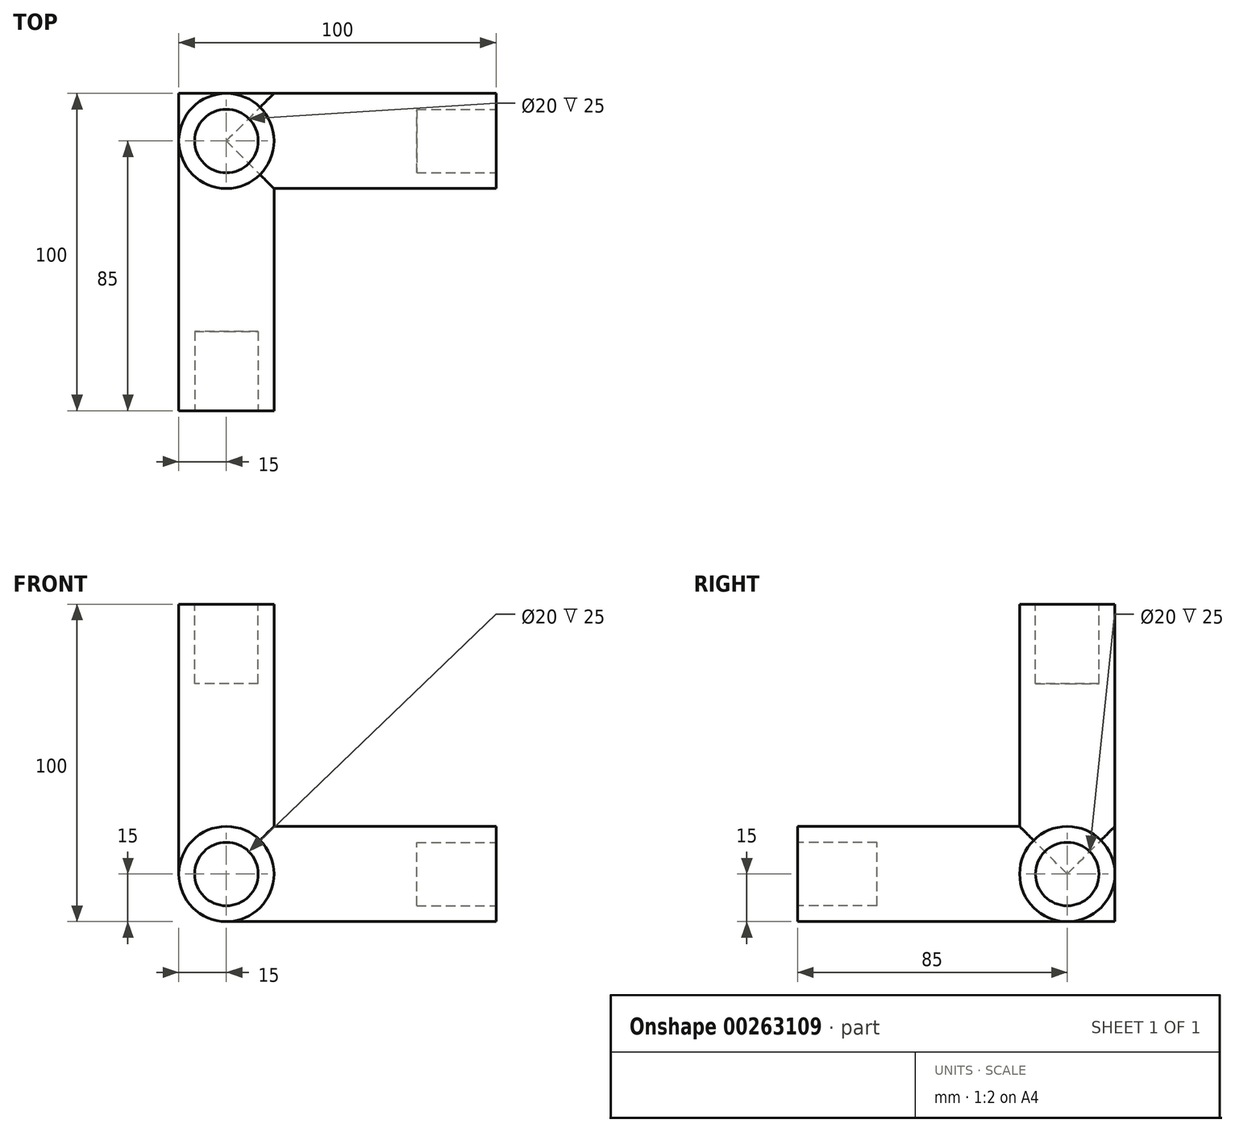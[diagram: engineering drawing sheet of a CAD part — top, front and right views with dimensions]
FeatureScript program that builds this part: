
annotation { "Feature Type Name" : "Feature", "Feature Type Description" : "" }
export const myFeature = defineFeature(function(context is Context, id is Id, definition is map)
    precondition{}
    {
        {
            assignVariable(context, id + "F0", {"name" : "large", "anyValue" : 100});
        }
        {
            assignVariable(context, id + "F1", {"name" : "hole", "anyValue" : 25});
        }
        {
            var Q0;
            Q0=qCreatedBy(makeId("Front.planeOp"),FACE);
            var sketch = newSketch(context, id + "F2", { "sketchPlane" : qUnion([Q0])});
            skCircle(sketch, "E0", {"center": v(0, 0) * mm, "radius": 15 * mm});
            skSolve(sketch);
        }
        {
            var Q0;
            Q0=makeQuery(id+"F2.imprint","IMPRINT",FACE,{"disambiguationData":[TD([[makeQuery(id+"F2.imprint","IMPRINT",EDGE,{"derivedFrom":sQuery(id+"F2.wireOp",EDGE,"E0")}),1.0]])]});
            extrude(context, id + "F3", {"entities" : qUnion([Q0]), "depth" : (getVariable(context, 'large')) * mm});
        }
        {
            var Q0;
            Q0=makeQuery(id+"F3.opExtrude","CAP_FACE",FACE,{"disambiguationData":[OSD([sQuery(id+"F2.wireOp",EDGE,"E0")])],"isStart":false});
            var sketch = newSketch(context, id + "F4", { "sketchPlane" : qUnion([Q0])});
            skCircle(sketch, "E1", {"center": v(0, 0) * mm, "radius": 10 * mm});
            skSolve(sketch);
        }
        {
            var Q0;
            Q0=makeQuery(id+"F4.imprint","IMPRINT",FACE,{"disambiguationData":[TD([[makeQuery(id+"F4.imprint","IMPRINT",EDGE,{"derivedFrom":sQuery(id+"F4.wireOp",EDGE,"E1")}),1.0]])]});
            extrude(context, id + "F5", {"entities" : qUnion([Q0]), "operationType" : NewBodyOperationType.REMOVE, "oppositeDirection" : true, "depth" : (getVariable(context, 'hole')) * mm});
        }
        {
            var Q0;
            Q0=qCreatedBy(makeId("Top.planeOp"),FACE);
            var sketch = newSketch(context, id + "F6", { "sketchPlane" : qUnion([Q0])});
            skPoint(sketch, "E2.middle", {"position": v(0, 0) * mm});
            skCircle(sketch, "E3", {"center": v(0, -15) * mm, "radius": 15 * mm});
            skPoint(sketch, "E3.second.point", {"position": v(0, -30) * mm});
            skPoint(sketch, "E3.third.point", {"position": v(-15, -15) * mm});
            skSolve(sketch);
        }
        {
            var Q0;
            Q0 = qSketchRegion(id + "F6", true);
            extrude(context, id + "F7", {"entities" : qUnion([Q0]), "operationType" : NewBodyOperationType.ADD, "depth" : ((.85) * (getVariable(context, 'large'))) * mm});
        }
        {
            var Q0;
            Q0=makeQuery(id+"F7.opExtrude","CAP_FACE",FACE,{"disambiguationData":[OSD([sQuery(id+"F6.wireOp",EDGE,"E3")])],"isStart":false});
            var sketch = newSketch(context, id + "F8", { "sketchPlane" : qUnion([Q0])});
            skCircle(sketch, "E4", {"center": v(0, -15) * mm, "radius": 10 * mm});
            skSolve(sketch);
        }
        {
            var Q0;
            Q0=makeQuery(id+"F8.imprint","IMPRINT",FACE,{"disambiguationData":[TD([[makeQuery(id+"F8.imprint","IMPRINT",EDGE,{"derivedFrom":sQuery(id+"F8.wireOp",EDGE,"E4")}),1.0]])]});
            extrude(context, id + "F9", {"entities" : qUnion([Q0]), "operationType" : NewBodyOperationType.REMOVE, "oppositeDirection" : true, "depth" : (getVariable(context, 'hole')) * mm});
        }
        {
            var Q0;
            Q0=qCreatedBy(makeId("Right.planeOp"),FACE);
            var sketch = newSketch(context, id + "F10", { "sketchPlane" : qUnion([Q0])});
            skCircle(sketch, "E5", {"center": v(-15, 0) * mm, "radius": 15 * mm});
            skPoint(sketch, "E5.third.point", {"position": v(-15, -15) * mm});
            skSolve(sketch);
        }
        {
            var Q0;
            Q0 = qSketchRegion(id + "F10", true);
            var Q1;
            Q1=sQuery(id+"F10.wireOp",EDGE,"E5");
            extrude(context, id + "F11", {"entities" : qUnion([Q0]), "operationType" : NewBodyOperationType.ADD, "surfaceEntities" : qUnion([Q1]), "depth" : ((0.85) * (getVariable(context, 'large'))) * mm});
        }
        {
            var Q0;
            Q0=makeQuery(id+"F11.opExtrude","CAP_FACE",FACE,{"disambiguationData":[OSD([sQuery(id+"F10.wireOp",EDGE,"E5")])],"isStart":false});
            var sketch = newSketch(context, id + "F12", { "sketchPlane" : qUnion([Q0])});
            skCircle(sketch, "E6", {"center": v(-15, 0) * mm, "radius": 10 * mm});
            skSolve(sketch);
        }
        {
            var Q0;
            Q0=makeQuery(id+"F12.imprint","IMPRINT",FACE,{"disambiguationData":[TD([[makeQuery(id+"F12.imprint","IMPRINT",EDGE,{"derivedFrom":sQuery(id+"F12.wireOp",EDGE,"E6")}),1.0]])]});
            extrude(context, id + "F13", {"entities" : qUnion([Q0]), "operationType" : NewBodyOperationType.REMOVE, "oppositeDirection" : true, "depth" : (getVariable(context, 'hole')) * mm});
        }
    });
